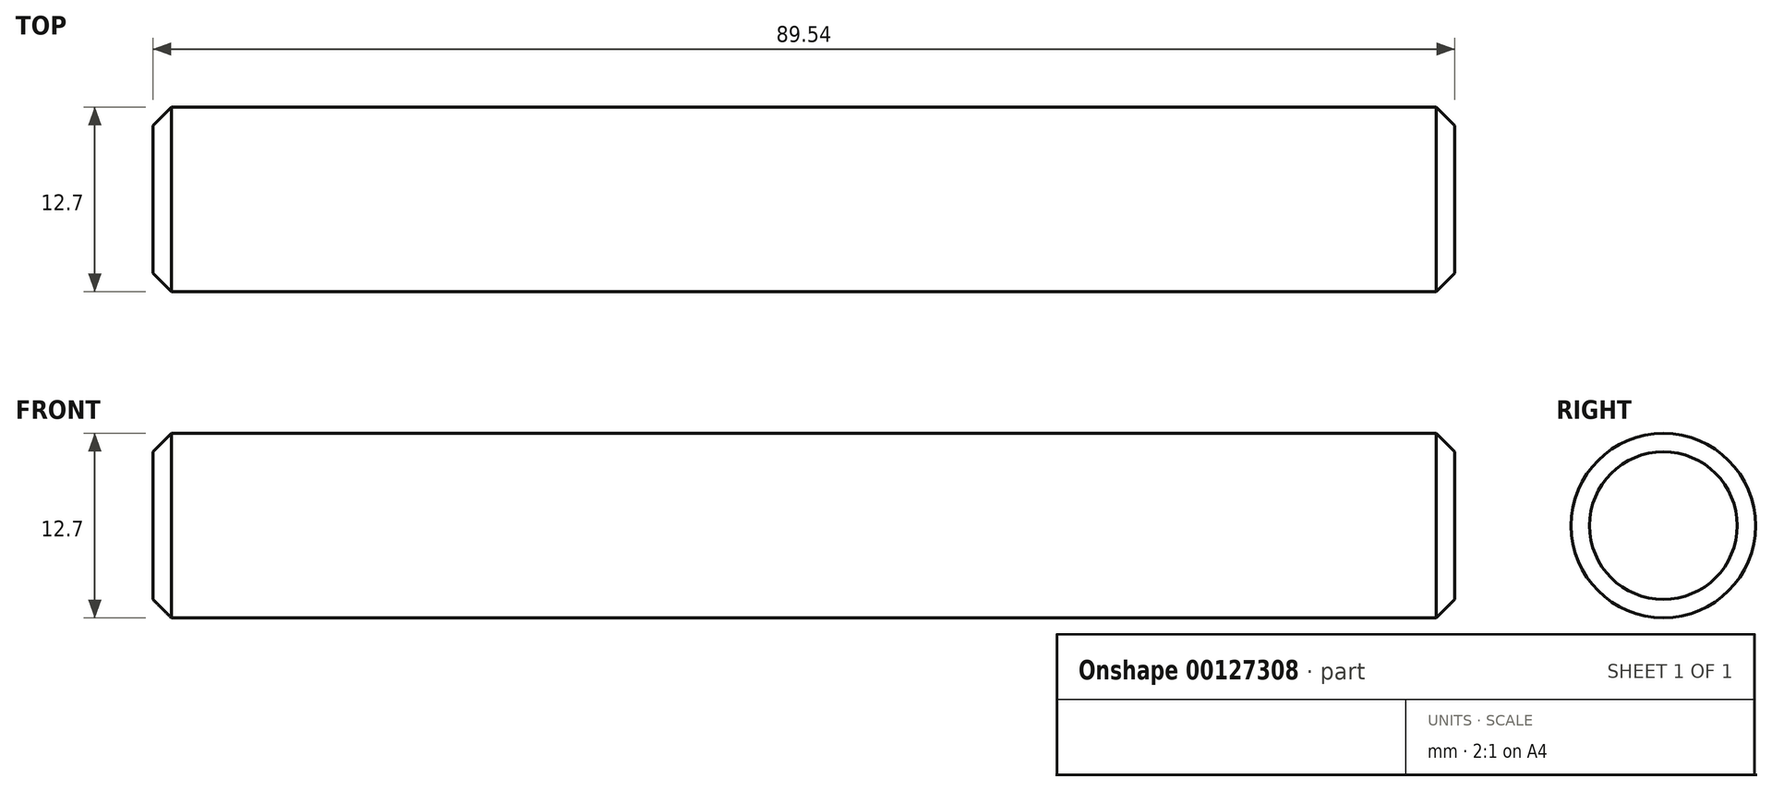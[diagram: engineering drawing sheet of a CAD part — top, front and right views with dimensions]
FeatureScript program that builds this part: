
annotation { "Feature Type Name" : "Feature", "Feature Type Description" : "" }
export const myFeature = defineFeature(function(context is Context, id is Id, definition is map)
    precondition{}
    {
        {
            var Q0;
            Q0=qCreatedBy(makeId("Right.planeOp"),FACE);
            var sketch = newSketch(context, id + "F0", { "sketchPlane" : qUnion([Q0])});
            skCircle(sketch, "E0", {"center": v(0, 0) * mm, "radius": 6.35 * mm});
            skSolve(sketch);
        }
        {
            var Q0;
            Q0 = qSketchRegion(id + "F0", true);
            extrude(context, id + "F1", {"entities" : qUnion([Q0]), "depth" : 89.53 * mm});
        }
        {
            var Q0;
            Q0=makeQuery(id+"F1.opExtrude","SWEPT_FACE",FACE,{"disambiguationData":[OSD([sQuery(id+"F0.wireOp",EDGE,"E0")])]});
            chamfer(context, id + "F2", {"entities" : qUnion([Q0]), "width" : 1.27 * mm, "tangentPropagation" : true});
        }
    });
